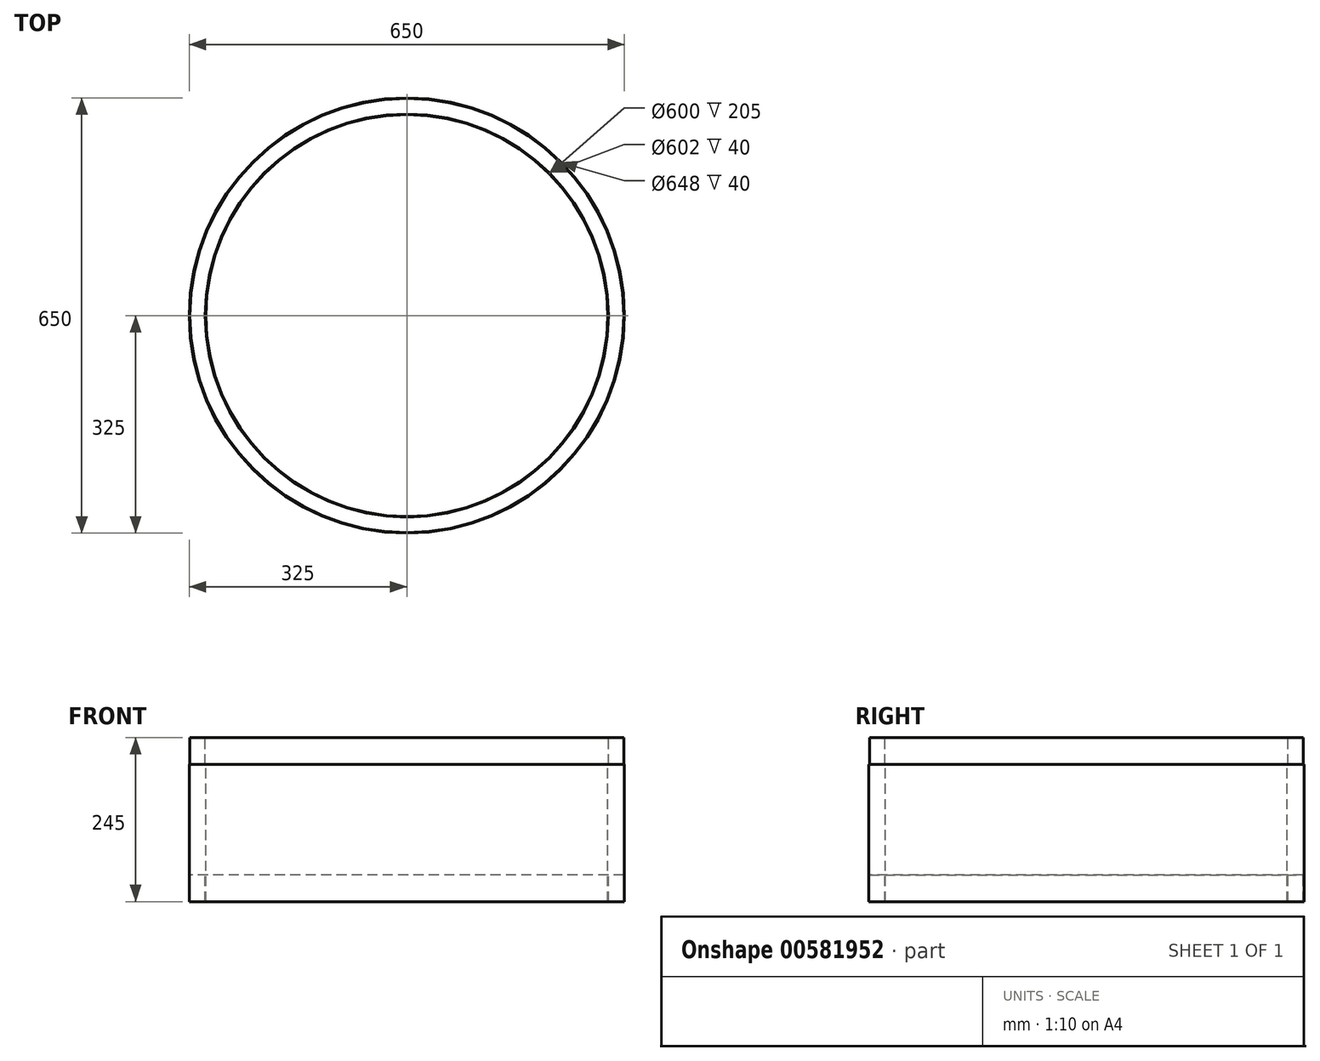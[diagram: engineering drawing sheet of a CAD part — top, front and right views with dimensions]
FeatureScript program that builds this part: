
annotation { "Feature Type Name" : "Feature", "Feature Type Description" : "" }
export const myFeature = defineFeature(function(context is Context, id is Id, definition is map)
    precondition{}
    {
        {
            var Q0;
            Q0=qCreatedBy(makeId("Front.planeOp"),FACE);
            var sketch = newSketch(context, id + "F0", { "sketchPlane" : qUnion([Q0])});
            skLineSegment(sketch, "E0", {"start": v(0, 345.75) * mm, "end": v(0, -558.03) * mm, "construction": true});
            skLineSegment(sketch, "E1", {"start": v(-300, -518.84) * mm, "end": v(-300, -313.84) * mm});
            skLineSegment(sketch, "E2", {"start": v(-300, -313.84) * mm, "end": v(-301, -313.84) * mm});
            skLineSegment(sketch, "E3", {"start": v(-301, -313.84) * mm, "end": v(-301, -273.84) * mm});
            skLineSegment(sketch, "E4", {"start": v(-301, -273.84) * mm, "end": v(-324, -273.84) * mm});
            skLineSegment(sketch, "E5", {"start": v(-324, -273.84) * mm, "end": v(-324, -313.84) * mm});
            skLineSegment(sketch, "E6", {"start": v(-324, -313.84) * mm, "end": v(-325, -313.84) * mm});
            skLineSegment(sketch, "E7", {"start": v(-325, -313.84) * mm, "end": v(-325, -518.84) * mm});
            skLineSegment(sketch, "E8", {"start": v(-325, -518.84) * mm, "end": v(-324, -518.84) * mm});
            skLineSegment(sketch, "E9", {"start": v(-324, -518.84) * mm, "end": v(-324, -478.84) * mm});
            skLineSegment(sketch, "E10", {"start": v(-324, -478.84) * mm, "end": v(-301, -478.84) * mm});
            skLineSegment(sketch, "E11", {"start": v(-301, -478.84) * mm, "end": v(-301, -518.84) * mm});
            skLineSegment(sketch, "E12", {"start": v(-301, -518.84) * mm, "end": v(-300, -518.84) * mm});
            skSolve(sketch);
        }
        {
            var Q0;
            Q0=qSketchRegion(id+"F0",true);
            var Q1;
            Q1=sQuery(id+"F0.wireOp",EDGE,"E0");
            revolve(context, id + "F1", {"entities" : qUnion([Q0]), "axis" : qUnion([Q1]), "revolveType" : RevolveType.FULL});
        }
    });
